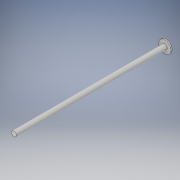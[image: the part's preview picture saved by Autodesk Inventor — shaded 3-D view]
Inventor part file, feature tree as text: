
AUTODESK INVENTOR PART (.ipt)
format: ipt  version: 2017 (Build 210142000, 142)  size: 102,912 bytes
history: native  units: in
note: dims shown in document units (in); Inventor stores cm internally (conversion verified against a paired STEP export)
features: extrude x4, sketch x4
ambient origin geometry x8: Origin, YZ Plane, XZ Plane, XY Plane, X Axis, Y Axis, Z Axis, Center Point
bodies: Solid1 (feature_tree)
feature tree (8):
  extrude  "Extrusion1"  Depth=11.75in TaperAngle=0.0deg
  extrude  "Extrusion2"  Depth=0.05in TaperAngle=0.0deg
  extrude  "Extrusion3"  Depth=0.1in TaperAngle=0.0deg
  extrude  "Extrusion4"  [1 undecoded]
  sketch  "Sketch1"  dims[d0=0.4in d1=11.75in d2=0.0in]
  sketch  "Sketch2"  dims[d3=0.125in d4=0.0in d5=0.05in d6=0.0in]
  sketch  "Sketch3"  dims[d7=1.0in d8=0.1in d9=0.0in]
  sketch  "Sketch4"
note: 1 required parameter value undecoded (feature->parameter linkage not recoverable at this tier; creation-order binding heuristic only, values carry confidence <= 0.55)
